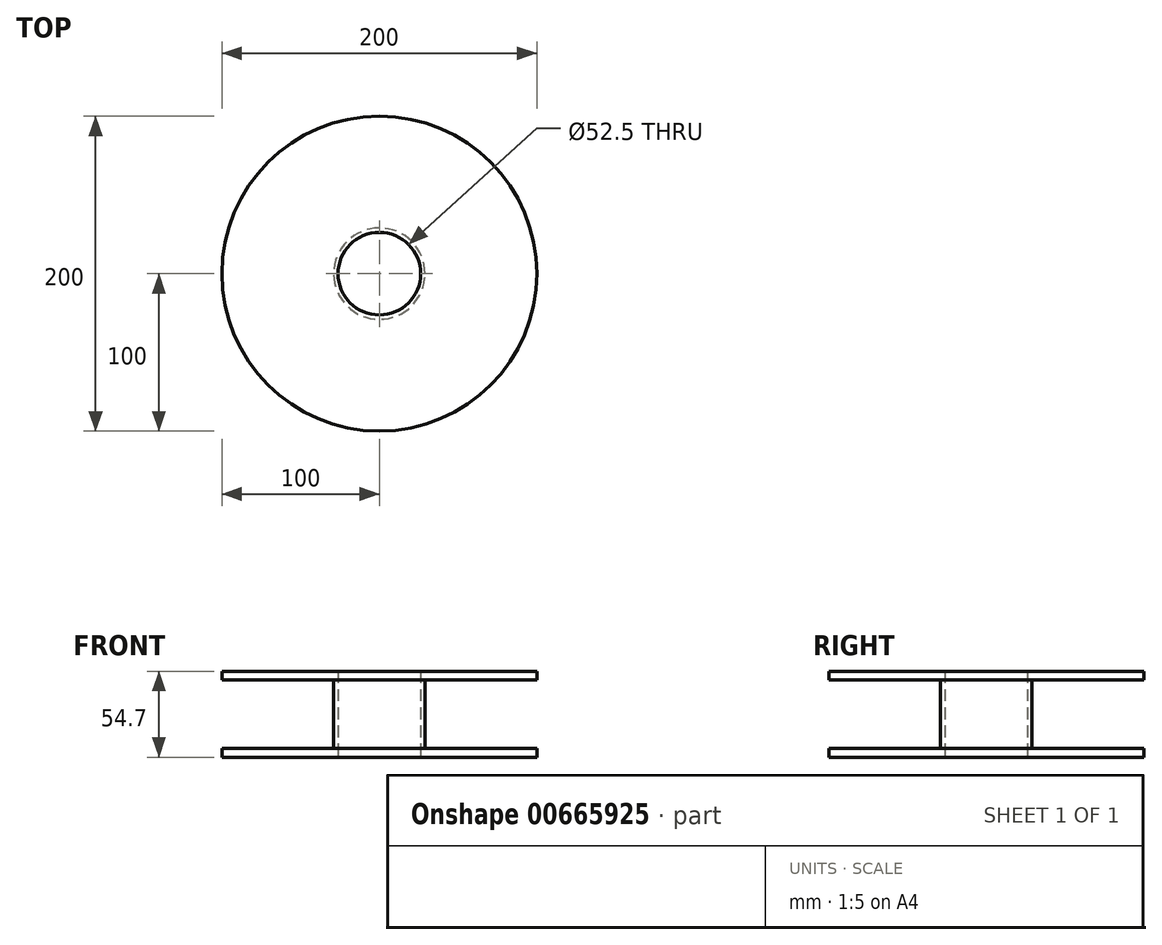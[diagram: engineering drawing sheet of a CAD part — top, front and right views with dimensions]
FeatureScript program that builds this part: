
annotation { "Feature Type Name" : "Feature", "Feature Type Description" : "" }
export const myFeature = defineFeature(function(context is Context, id is Id, definition is map)
    precondition{}
    {
        {
            var Q0;
            Q0=qCreatedBy(makeId("Top.planeOp"),FACE);
            var sketch = newSketch(context, id + "F0", { "sketchPlane" : qUnion([Q0])});
            skCircle(sketch, "E0", {"center": v(0, 0) * mm, "radius": 100 * mm});
            skCircle(sketch, "E1", {"center": v(0, 0) * mm, "radius": 26.25 * mm});
            skSolve(sketch);
        }
        {
            var Q0;
            Q0 = qSketchRegion(id + "F0", true);
            extrude(context, id + "F1", {"entities" : qUnion([Q0]), "depth" : 5.6 * mm, "offsetDistance" : 25 * mm});
        }
        {
            var Q0;
            Q0=makeQuery(id+"F1.opExtrude","CAP_FACE",FACE,{"disambiguationData":[OSD([sQuery(id+"F0.wireOp",EDGE,"E0")])],"isStart":false});
            var sketch = newSketch(context, id + "F2", { "sketchPlane" : qUnion([Q0])});
            skCircle(sketch, "E2", {"center": v(0, 0) * mm, "radius": 29 * mm});
            skCircle(sketch, "E3.0", {"center": v(0, 0) * mm, "radius": 26.25 * mm});
            skSolve(sketch);
        }
        {
            var Q0;
            Q0 = qSketchRegion(id + "F2", true);
            extrude(context, id + "F3", {"entities" : qUnion([Q0]), "operationType" : NewBodyOperationType.ADD, "depth" : 43.5 * mm, "offsetDistance" : 25 * mm});
        }
        {
            var Q0;
            Q0=makeQuery(id+"F3.opExtrude","CAP_FACE",FACE,{"disambiguationData":[OSD([sQuery(id+"F2.wireOp",EDGE,"E2")])],"isStart":false});
            var sketch = newSketch(context, id + "F4", { "sketchPlane" : qUnion([Q0])});
            skCircle(sketch, "E4.0", {"center": v(0, 0) * mm, "radius": 100 * mm});
            skCircle(sketch, "E5.0", {"center": v(0, 0) * mm, "radius": 26.25 * mm});
            skSolve(sketch);
        }
        {
            var Q0;
            Q0 = qSketchRegion(id + "F4", true);
            extrude(context, id + "F5", {"entities" : qUnion([Q0]), "operationType" : NewBodyOperationType.ADD, "depth" : 5.6 * mm, "offsetDistance" : 25 * mm});
        }
    });
